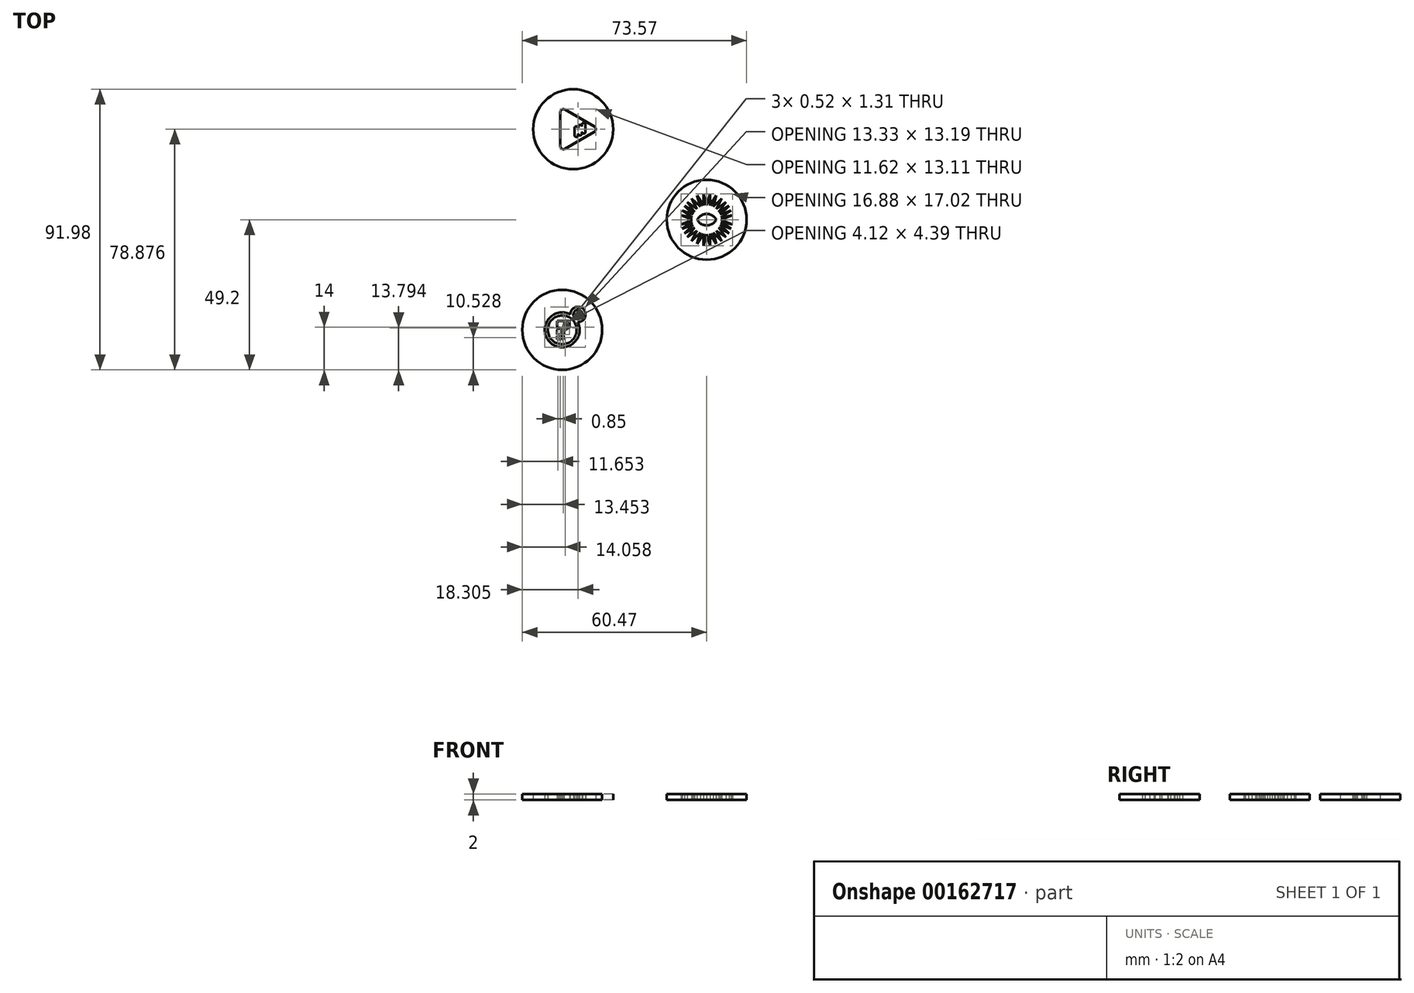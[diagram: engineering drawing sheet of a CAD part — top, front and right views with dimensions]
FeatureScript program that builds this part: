
annotation { "Feature Type Name" : "Feature", "Feature Type Description" : "" }
export const myFeature = defineFeature(function(context is Context, id is Id, definition is map)
    precondition{}
    {
        {
            var Q0;
            Q0=qCreatedBy(makeId("Top.planeOp"),FACE);
            var sketch = newSketch(context, id + "F0", { "sketchPlane" : qUnion([Q0])});
            skCircle(sketch, "E0", {"center": v(0, 0) * mm, "radius": 13.1 * mm});
            skLineSegment(sketch, "E1", {"start": v(0, 4.73) * mm, "end": v(1.07, 8.5) * mm});
            skLineSegment(sketch, "E2", {"start": v(1.07, 8.5) * mm, "end": v(1.07, 4.6) * mm});
            skLineSegment(sketch, "E3", {"start": v(1.07, 4.6) * mm, "end": v(3.18, 7.97) * mm});
            skLineSegment(sketch, "E4", {"start": v(3.18, 7.97) * mm, "end": v(2.11, 4.23) * mm});
            skLineSegment(sketch, "E5", {"start": v(2.11, 4.23) * mm, "end": v(4.97, 7) * mm});
            skLineSegment(sketch, "E6", {"start": v(4.97, 7) * mm, "end": v(3.14, 3.54) * mm});
            skLineSegment(sketch, "E7", {"start": v(3.14, 3.54) * mm, "end": v(6.35, 5.77) * mm});
            skLineSegment(sketch, "E8", {"start": v(6.35, 5.77) * mm, "end": v(3.97, 2.57) * mm});
            skLineSegment(sketch, "E9", {"start": v(3.97, 2.57) * mm, "end": v(7.3, 4.5) * mm});
            skLineSegment(sketch, "E10", {"start": v(7.3, 4.5) * mm, "end": v(4.4, 1.73) * mm});
            skLineSegment(sketch, "E11", {"start": v(4.4, 1.73) * mm, "end": v(8.03, 3) * mm});
            skLineSegment(sketch, "E12", {"start": v(8.03, 3) * mm, "end": v(4.66, 0.79) * mm});
            skLineSegment(sketch, "E13", {"start": v(4.66, 0.79) * mm, "end": v(8.44, 1.53) * mm});
            skLineSegment(sketch, "E14", {"start": v(8.44, 1.53) * mm, "end": v(4.73, 0) * mm});
            skLineSegment(sketch, "E15", {"start": v(4.73, 0) * mm, "end": v(8.58, 0) * mm});
            skLineSegment(sketch, "E16.MirrorCS", {"start": v(-4.73, 0) * mm, "end": v(-8.58, 0) * mm});
            skLineSegment(sketch, "E17.MirrorCS", {"start": v(-8.44, 1.53) * mm, "end": v(-4.73, 0) * mm});
            skLineSegment(sketch, "E18.MirrorCS", {"start": v(-4.66, 0.79) * mm, "end": v(-8.44, 1.53) * mm});
            skLineSegment(sketch, "E19.MirrorCS", {"start": v(-8.03, 3) * mm, "end": v(-4.66, 0.79) * mm});
            skLineSegment(sketch, "E20.MirrorCS", {"start": v(-4.4, 1.73) * mm, "end": v(-8.03, 3) * mm});
            skLineSegment(sketch, "E21.MirrorCS", {"start": v(-7.3, 4.5) * mm, "end": v(-4.4, 1.73) * mm});
            skLineSegment(sketch, "E22.MirrorCS", {"start": v(-3.97, 2.57) * mm, "end": v(-7.3, 4.5) * mm});
            skLineSegment(sketch, "E23.MirrorCS", {"start": v(-6.35, 5.77) * mm, "end": v(-3.97, 2.57) * mm});
            skLineSegment(sketch, "E24.MirrorCS", {"start": v(-3.14, 3.54) * mm, "end": v(-6.35, 5.77) * mm});
            skLineSegment(sketch, "E25.MirrorCS", {"start": v(-4.97, 7) * mm, "end": v(-3.14, 3.54) * mm});
            skLineSegment(sketch, "E26.MirrorCS", {"start": v(-2.11, 4.23) * mm, "end": v(-4.97, 7) * mm});
            skLineSegment(sketch, "E27.MirrorCS", {"start": v(-3.18, 7.97) * mm, "end": v(-2.11, 4.23) * mm});
            skLineSegment(sketch, "E28.MirrorCS", {"start": v(-1.07, 4.6) * mm, "end": v(-3.18, 7.97) * mm});
            skLineSegment(sketch, "E29.MirrorCS", {"start": v(0, 4.73) * mm, "end": v(-1.07, 8.5) * mm});
            skLineSegment(sketch, "E30.MirrorCS", {"start": v(-1.07, 8.5) * mm, "end": v(-1.07, 4.6) * mm});
            skLineSegment(sketch, "E31.MirrorCS", {"start": v(8.44, -1.53) * mm, "end": v(4.73, 0) * mm});
            skLineSegment(sketch, "E32.MirrorCS", {"start": v(4.66, -0.79) * mm, "end": v(8.44, -1.53) * mm});
            skLineSegment(sketch, "E33.MirrorCS", {"start": v(8.03, -3) * mm, "end": v(4.66, -0.79) * mm});
            skLineSegment(sketch, "E34.MirrorCS", {"start": v(4.4, -1.73) * mm, "end": v(8.03, -3) * mm});
            skLineSegment(sketch, "E35.MirrorCS", {"start": v(7.3, -4.5) * mm, "end": v(4.4, -1.73) * mm});
            skLineSegment(sketch, "E36.MirrorCS", {"start": v(3.97, -2.57) * mm, "end": v(7.3, -4.5) * mm});
            skLineSegment(sketch, "E37.MirrorCS", {"start": v(6.35, -5.77) * mm, "end": v(3.97, -2.57) * mm});
            skLineSegment(sketch, "E38.MirrorCS", {"start": v(3.14, -3.54) * mm, "end": v(6.35, -5.77) * mm});
            skLineSegment(sketch, "E39.MirrorCS", {"start": v(4.97, -7) * mm, "end": v(3.14, -3.54) * mm});
            skLineSegment(sketch, "E40.MirrorCS", {"start": v(2.11, -4.23) * mm, "end": v(4.97, -7) * mm});
            skLineSegment(sketch, "E41.MirrorCS", {"start": v(3.18, -7.97) * mm, "end": v(2.11, -4.23) * mm});
            skLineSegment(sketch, "E42.MirrorCS", {"start": v(1.07, -4.6) * mm, "end": v(3.18, -7.97) * mm});
            skLineSegment(sketch, "E43.MirrorCS", {"start": v(1.07, -8.5) * mm, "end": v(1.07, -4.6) * mm});
            skLineSegment(sketch, "E44.MirrorCS", {"start": v(0, -4.73) * mm, "end": v(1.07, -8.5) * mm});
            skLineSegment(sketch, "E45.MirrorCS", {"start": v(0, -4.73) * mm, "end": v(-1.07, -8.5) * mm});
            skLineSegment(sketch, "E46.MirrorCS", {"start": v(-1.07, -8.5) * mm, "end": v(-1.07, -4.6) * mm});
            skLineSegment(sketch, "E47.MirrorCS", {"start": v(-1.07, -4.6) * mm, "end": v(-3.18, -7.97) * mm});
            skLineSegment(sketch, "E48.MirrorCS", {"start": v(-3.18, -7.97) * mm, "end": v(-2.11, -4.23) * mm});
            skLineSegment(sketch, "E49.MirrorCS", {"start": v(-2.11, -4.23) * mm, "end": v(-4.97, -7) * mm});
            skLineSegment(sketch, "E50.MirrorCS", {"start": v(-4.97, -7) * mm, "end": v(-3.14, -3.54) * mm});
            skLineSegment(sketch, "E51.MirrorCS", {"start": v(-3.14, -3.54) * mm, "end": v(-6.35, -5.77) * mm});
            skLineSegment(sketch, "E52.MirrorCS", {"start": v(-6.35, -5.77) * mm, "end": v(-3.97, -2.57) * mm});
            skLineSegment(sketch, "E53.MirrorCS", {"start": v(-3.97, -2.57) * mm, "end": v(-7.3, -4.5) * mm});
            skLineSegment(sketch, "E54.MirrorCS", {"start": v(-7.3, -4.5) * mm, "end": v(-4.4, -1.73) * mm});
            skLineSegment(sketch, "E55.MirrorCS", {"start": v(-4.4, -1.73) * mm, "end": v(-8.03, -3) * mm});
            skLineSegment(sketch, "E56.MirrorCS", {"start": v(-8.03, -3) * mm, "end": v(-4.66, -0.79) * mm});
            skLineSegment(sketch, "E57.MirrorCS", {"start": v(-4.66, -0.79) * mm, "end": v(-8.44, -1.53) * mm});
            skLineSegment(sketch, "E58.MirrorCS", {"start": v(-8.44, -1.53) * mm, "end": v(-4.73, 0) * mm});
            skSolve(sketch);
        }
        {
            var Q0;
            Q0=makeQuery(id+"F0.imprint","IMPRINT",FACE,{"disambiguationData":[TD([[makeQuery(id+"F0.imprint","IMPRINT",EDGE,{"derivedFrom":sQuery(id+"F0.wireOp",EDGE,"E0")}),1.0]])]});
            extrude(context, id + "F1", {"entities" : qUnion([Q0]), "depth" : 2 * mm});
        }
        {
            var Q0;
            Q0=qCreatedBy(makeId("Top.planeOp"),FACE);
            var sketch = newSketch(context, id + "F2", { "sketchPlane" : qUnion([Q0])});
            skCircle(sketch, "E59", {"center": v(-43.77, 29.68) * mm, "radius": 13.1 * mm});
            skCircle(sketch, "E60.cCircle", {"center": v(-43.77, 29.68) * mm, "radius": 8.41 * mm, "construction": true});
            skLineSegment(sketch, "E60.0", {"start": v(-36.85, 28.81) * mm, "end": v(-46.48, 23.25) * mm});
            skLineSegment(sketch, "E60.1", {"start": v(-47.98, 24.12) * mm, "end": v(-47.98, 35.23) * mm});
            skLineSegment(sketch, "E60.2", {"start": v(-46.48, 36.1) * mm, "end": v(-36.85, 30.54) * mm});
            skPoint(sketch, "E61.visualSharp", {"position": v(-47.98, 36.96) * mm});
            skArc(sketch, "E61.filletArc", {"start": v(-46.48, 36.1) * mm, "mid": v(-47.48, 36.1) * mm, "end": v(-47.98, 35.23) * mm});
            skPoint(sketch, "E62.visualSharp", {"position": v(-47.98, 22.39) * mm});
            skArc(sketch, "E62.filletArc", {"start": v(-47.98, 24.12) * mm, "mid": v(-47.48, 23.25) * mm, "end": v(-46.48, 23.25) * mm});
            skPoint(sketch, "E63.visualSharp", {"position": v(-35.35, 29.68) * mm});
            skArc(sketch, "E63.filletArc", {"start": v(-36.85, 28.81) * mm, "mid": v(-36.35, 29.68) * mm, "end": v(-36.85, 30.54) * mm});
            skLineSegment(sketch, "E64.bottom", {"start": v(-40.24, 31.72) * mm, "end": v(-40.37, 31.72) * mm});
            skLineSegment(sketch, "E64.top", {"start": v(-40.24, 28.26) * mm, "end": v(-40.37, 28.26) * mm});
            skLineSegment(sketch, "E64.left", {"start": v(-39.74, 31.22) * mm, "end": v(-39.74, 28.76) * mm});
            skLineSegment(sketch, "E64.right", {"start": v(-40.87, 31.22) * mm, "end": v(-40.87, 30.61) * mm});
            skPoint(sketch, "E65.visualSharp", {"position": v(-40.87, 31.72) * mm});
            skArc(sketch, "E65.filletArc", {"start": v(-40.37, 31.72) * mm, "mid": v(-40.72, 31.57) * mm, "end": v(-40.87, 31.22) * mm});
            skPoint(sketch, "E66.visualSharp", {"position": v(-39.74, 28.26) * mm});
            skArc(sketch, "E66.filletArc", {"start": v(-40.24, 28.26) * mm, "mid": v(-39.88, 28.4) * mm, "end": v(-39.74, 28.76) * mm});
            skPoint(sketch, "E67.visualSharp", {"position": v(-40.87, 28.26) * mm});
            skArc(sketch, "E67.filletArc", {"start": v(-40.87, 28.76) * mm, "mid": v(-40.72, 28.4) * mm, "end": v(-40.37, 28.26) * mm});
            skPoint(sketch, "E68.visualSharp", {"position": v(-39.74, 31.72) * mm});
            skArc(sketch, "E68.filletArc", {"start": v(-39.74, 31.22) * mm, "mid": v(-39.88, 31.57) * mm, "end": v(-40.24, 31.72) * mm});
            skPoint(sketch, "E69", {"position": v(-22.66, 22.26) * mm});
            skLineSegment(sketch, "E70.bottom", {"start": v(-41.45, 31.11) * mm, "end": v(-41.58, 31.11) * mm});
            skLineSegment(sketch, "E70.top", {"start": v(-41.45, 27.66) * mm, "end": v(-41.58, 27.66) * mm});
            skLineSegment(sketch, "E70.left", {"start": v(-40.95, 28.76) * mm, "end": v(-40.95, 28.16) * mm});
            skLineSegment(sketch, "E70.right", {"start": v(-42.08, 30.61) * mm, "end": v(-42.08, 30.12) * mm});
            skPoint(sketch, "E71.visualSharp", {"position": v(-42.08, 31.11) * mm});
            skArc(sketch, "E71.filletArc", {"start": v(-41.58, 31.11) * mm, "mid": v(-41.94, 30.97) * mm, "end": v(-42.08, 30.61) * mm});
            skPoint(sketch, "E72.visualSharp", {"position": v(-40.95, 27.66) * mm});
            skArc(sketch, "E72.filletArc", {"start": v(-41.45, 27.66) * mm, "mid": v(-41.1, 27.8) * mm, "end": v(-40.95, 28.16) * mm});
            skPoint(sketch, "E73.visualSharp", {"position": v(-42.08, 27.66) * mm});
            skArc(sketch, "E73.filletArc", {"start": v(-42.08, 28.16) * mm, "mid": v(-41.94, 27.8) * mm, "end": v(-41.58, 27.66) * mm});
            skPoint(sketch, "E74.visualSharp", {"position": v(-40.95, 31.11) * mm});
            skArc(sketch, "E74.filletArc", {"start": v(-40.95, 30.61) * mm, "mid": v(-41.1, 30.97) * mm, "end": v(-41.45, 31.11) * mm});
            skLineSegment(sketch, "E75.bottom", {"start": v(-42.68, 30.62) * mm, "end": v(-42.81, 30.62) * mm});
            skLineSegment(sketch, "E75.top", {"start": v(-42.68, 27.16) * mm, "end": v(-42.81, 27.16) * mm});
            skLineSegment(sketch, "E75.left", {"start": v(-42.18, 28.16) * mm, "end": v(-42.18, 27.66) * mm});
            skLineSegment(sketch, "E75.right", {"start": v(-43.31, 30.12) * mm, "end": v(-43.31, 27.66) * mm});
            skPoint(sketch, "E76.visualSharp", {"position": v(-43.31, 30.62) * mm});
            skArc(sketch, "E76.filletArc", {"start": v(-42.81, 30.62) * mm, "mid": v(-43.16, 30.47) * mm, "end": v(-43.31, 30.12) * mm});
            skPoint(sketch, "E77.visualSharp", {"position": v(-42.18, 27.16) * mm});
            skArc(sketch, "E77.filletArc", {"start": v(-42.68, 27.16) * mm, "mid": v(-42.33, 27.3) * mm, "end": v(-42.18, 27.66) * mm});
            skPoint(sketch, "E78.visualSharp", {"position": v(-43.31, 27.16) * mm});
            skArc(sketch, "E78.filletArc", {"start": v(-43.31, 27.66) * mm, "mid": v(-43.16, 27.3) * mm, "end": v(-42.81, 27.16) * mm});
            skPoint(sketch, "E79.visualSharp", {"position": v(-42.18, 30.62) * mm});
            skArc(sketch, "E79.filletArc", {"start": v(-42.18, 30.12) * mm, "mid": v(-42.33, 30.47) * mm, "end": v(-42.68, 30.62) * mm});
            skLineSegment(sketch, "E80", {"start": v(-42.08, 28.16) * mm, "end": v(-42.18, 28.16) * mm});
            skLineSegment(sketch, "E81", {"start": v(-42.08, 30.12) * mm, "end": v(-42.18, 30.12) * mm});
            skLineSegment(sketch, "E82", {"start": v(-40.95, 30.61) * mm, "end": v(-40.87, 30.61) * mm});
            skLineSegment(sketch, "E83", {"start": v(-40.95, 28.76) * mm, "end": v(-40.87, 28.76) * mm});
            skSolve(sketch);
        }
        {
            var Q0;
            Q0=makeQuery(id+"F2.imprint","IMPRINT",FACE,{"disambiguationData":[TD([[makeQuery(id+"F2.imprint","IMPRINT",EDGE,{"derivedFrom":sQuery(id+"F2.wireOp",EDGE,"E64.bottom")}),1.0]])]});
            var Q1;
            Q1=makeQuery(id+"F2.imprint","IMPRINT",FACE,{"disambiguationData":[TD([[makeQuery(id+"F2.imprint","IMPRINT",EDGE,{"derivedFrom":sQuery(id+"F2.wireOp",EDGE,"E59")}),1.0]])]});
            extrude(context, id + "F3", {"entities" : qUnion([Q0, Q1]), "depth" : 2 * mm});
        }
        {
            var Q0;
            Q0=qCreatedBy(makeId("Top.planeOp"),FACE);
            var sketch = newSketch(context, id + "F4", { "sketchPlane" : qUnion([Q0])});
            skCircle(sketch, "E84", {"center": v(-47.37, -36.1) * mm, "radius": 13.1 * mm});
            skCircle(sketch, "E85", {"center": v(-42.2, -31.05) * mm, "radius": 1.5 * mm});
            skArc(sketch, "E86", {"start": v(-42.25, -33.55) * mm, "mid": v(-40.42, -29.3) * mm, "end": v(-44.7, -31.04) * mm});
            skCircle(sketch, "E87", {"center": v(-47.37, -36.1) * mm, "radius": 4.72 * mm});
            skArc(sketch, "E88", {"start": v(-44.7, -31.04) * mm, "mid": v(-51.46, -40.1) * mm, "end": v(-42.25, -33.55) * mm});
            skLineSegment(sketch, "E89.bottom", {"start": v(-44.95, -33.21) * mm, "end": v(-49.08, -33.21) * mm});
            skLineSegment(sketch, "E89.top", {"start": v(-44.95, -35.44) * mm, "end": v(-45.79, -35.44) * mm});
            skLineSegment(sketch, "E89.left", {"start": v(-44.95, -33.21) * mm, "end": v(-44.95, -35.44) * mm});
            skLineSegment(sketch, "E89.right", {"start": v(-49.08, -33.21) * mm, "end": v(-49.08, -35.44) * mm});
            skLineSegment(sketch, "E90.bottom", {"start": v(-49.08, -33.21) * mm, "end": v(-46.79, -33.21) * mm});
            skLineSegment(sketch, "E90.top", {"start": v(-49.08, -37.6) * mm, "end": v(-46.79, -37.6) * mm});
            skLineSegment(sketch, "E90.right", {"start": v(-46.79, -36.44) * mm, "end": v(-46.79, -37.6) * mm});
            skLineSegment(sketch, "E91", {"start": v(-49.08, -35.44) * mm, "end": v(-48.1, -35.44) * mm});
            skLineSegment(sketch, "E92", {"start": v(-48.1, -35.44) * mm, "end": v(-49.08, -36.1) * mm});
            skPoint(sketch, "E92.endSnap0", {"position": v(-49.08, -34.33) * mm});
            skLineSegment(sketch, "E93.trimOffspring", {"start": v(-49.08, -36.1) * mm, "end": v(-49.08, -37.6) * mm});
            skLineSegment(sketch, "E94.bottom", {"start": v(-49.08, -38.02) * mm, "end": v(-48.56, -38.02) * mm});
            skLineSegment(sketch, "E94.top", {"start": v(-49.08, -39.33) * mm, "end": v(-48.56, -39.33) * mm});
            skLineSegment(sketch, "E94.left", {"start": v(-49.08, -38.02) * mm, "end": v(-49.08, -39.33) * mm});
            skLineSegment(sketch, "E94.right", {"start": v(-48.56, -38.02) * mm, "end": v(-48.56, -39.33) * mm});
            skLineSegment(sketch, "E95.bottom", {"start": v(-48.23, -38) * mm, "end": v(-47.7, -38) * mm});
            skLineSegment(sketch, "E95.top", {"start": v(-48.23, -39.32) * mm, "end": v(-47.7, -39.32) * mm});
            skLineSegment(sketch, "E95.left", {"start": v(-48.23, -38) * mm, "end": v(-48.23, -39.32) * mm});
            skLineSegment(sketch, "E95.right", {"start": v(-47.7, -38) * mm, "end": v(-47.7, -39.32) * mm});
            skLineSegment(sketch, "E96.bottom", {"start": v(-47.37, -37.98) * mm, "end": v(-46.85, -37.98) * mm});
            skLineSegment(sketch, "E96.top", {"start": v(-47.37, -39.3) * mm, "end": v(-46.85, -39.3) * mm});
            skLineSegment(sketch, "E96.left", {"start": v(-47.37, -37.98) * mm, "end": v(-47.37, -39.3) * mm});
            skLineSegment(sketch, "E96.right", {"start": v(-46.85, -37.98) * mm, "end": v(-46.85, -39.3) * mm});
            skPoint(sketch, "E97.visualSharp", {"position": v(-46.79, -35.44) * mm});
            skArc(sketch, "E97.filletArc", {"start": v(-45.79, -35.44) * mm, "mid": v(-46.5, -35.73) * mm, "end": v(-46.79, -36.44) * mm});
            skSolve(sketch);
        }
        {
            var Q0;
            Q0=makeQuery(id+"F4.imprint","IMPRINT",FACE,{"disambiguationData":[TD([[makeQuery(id+"F4.imprint","IMPRINT",EDGE,{"derivedFrom":sQuery(id+"F4.wireOp",EDGE,"E84")}),1.0]])]});
            var Q1;
            Q1=makeQuery(id+"F4.imprint","IMPRINT",FACE,{"disambiguationData":[TD([[makeQuery(id+"F4.imprint","IMPRINT",EDGE,{"derivedFrom":sQuery(id+"F4.wireOp",EDGE,"E85")}),1.0]])]});
            var Q2;
            Q2=makeQuery(id+"F4.imprint","IMPRINT",FACE,{"disambiguationData":[TD([[makeQuery(id+"F4.imprint","IMPRINT",EDGE,{"derivedFrom":sQuery(id+"F4.wireOp",EDGE,"E87")}),1.0]])]});
            extrude(context, id + "F5", {"entities" : qUnion([Q0, Q1, Q2]), "depth" : 2 * mm});
        }
        {
            var Q0;
            Q0=makeQuery(id+"F1.opExtrude","CAP_FACE",FACE,{"disambiguationData":[OSD([sQuery(id+"F0.wireOp",EDGE,"E0"),sQuery(id+"F0.wireOp",EDGE,"E1"),sQuery(id+"F0.wireOp",EDGE,"E2"),sQuery(id+"F0.wireOp",EDGE,"E3"),sQuery(id+"F0.wireOp",EDGE,"E4"),sQuery(id+"F0.wireOp",EDGE,"E5"),sQuery(id+"F0.wireOp",EDGE,"E6"),sQuery(id+"F0.wireOp",EDGE,"E7"),sQuery(id+"F0.wireOp",EDGE,"E8"),sQuery(id+"F0.wireOp",EDGE,"E9"),sQuery(id+"F0.wireOp",EDGE,"E10"),sQuery(id+"F0.wireOp",EDGE,"E11"),sQuery(id+"F0.wireOp",EDGE,"E12"),sQuery(id+"F0.wireOp",EDGE,"E13"),sQuery(id+"F0.wireOp",EDGE,"E14"),sQuery(id+"F0.wireOp",EDGE,"E19.MirrorCS"),sQuery(id+"F0.wireOp",EDGE,"E20.MirrorCS"),sQuery(id+"F0.wireOp",EDGE,"E21.MirrorCS"),sQuery(id+"F0.wireOp",EDGE,"E22.MirrorCS"),sQuery(id+"F0.wireOp",EDGE,"E23.MirrorCS"),sQuery(id+"F0.wireOp",EDGE,"E24.MirrorCS"),sQuery(id+"F0.wireOp",EDGE,"E25.MirrorCS"),sQuery(id+"F0.wireOp",EDGE,"E26.MirrorCS"),sQuery(id+"F0.wireOp",EDGE,"E27.MirrorCS"),sQuery(id+"F0.wireOp",EDGE,"E28.MirrorCS"),sQuery(id+"F0.wireOp",EDGE,"E29.MirrorCS"),sQuery(id+"F0.wireOp",EDGE,"E30.MirrorCS"),sQuery(id+"F0.wireOp",EDGE,"E18.MirrorCS"),sQuery(id+"F0.wireOp",EDGE,"E17.MirrorCS"),sQuery(id+"F0.wireOp",EDGE,"E31.MirrorCS"),sQuery(id+"F0.wireOp",EDGE,"E32.MirrorCS"),sQuery(id+"F0.wireOp",EDGE,"E33.MirrorCS"),sQuery(id+"F0.wireOp",EDGE,"E34.MirrorCS"),sQuery(id+"F0.wireOp",EDGE,"E35.MirrorCS"),sQuery(id+"F0.wireOp",EDGE,"E36.MirrorCS"),sQuery(id+"F0.wireOp",EDGE,"E37.MirrorCS"),sQuery(id+"F0.wireOp",EDGE,"E38.MirrorCS"),sQuery(id+"F0.wireOp",EDGE,"E39.MirrorCS"),sQuery(id+"F0.wireOp",EDGE,"E40.MirrorCS"),sQuery(id+"F0.wireOp",EDGE,"E41.MirrorCS"),sQuery(id+"F0.wireOp",EDGE,"E42.MirrorCS"),sQuery(id+"F0.wireOp",EDGE,"E43.MirrorCS"),sQuery(id+"F0.wireOp",EDGE,"E44.MirrorCS"),sQuery(id+"F0.wireOp",EDGE,"E45.MirrorCS"),sQuery(id+"F0.wireOp",EDGE,"E46.MirrorCS"),sQuery(id+"F0.wireOp",EDGE,"E47.MirrorCS"),sQuery(id+"F0.wireOp",EDGE,"E48.MirrorCS"),sQuery(id+"F0.wireOp",EDGE,"E49.MirrorCS"),sQuery(id+"F0.wireOp",EDGE,"E50.MirrorCS"),sQuery(id+"F0.wireOp",EDGE,"E51.MirrorCS"),sQuery(id+"F0.wireOp",EDGE,"E52.MirrorCS"),sQuery(id+"F0.wireOp",EDGE,"E53.MirrorCS"),sQuery(id+"F0.wireOp",EDGE,"E54.MirrorCS"),sQuery(id+"F0.wireOp",EDGE,"E55.MirrorCS"),sQuery(id+"F0.wireOp",EDGE,"E56.MirrorCS"),sQuery(id+"F0.wireOp",EDGE,"E57.MirrorCS"),sQuery(id+"F0.wireOp",EDGE,"E58.MirrorCS")])],"isStart":false});
            var sketch = newSketch(context, id + "F6", { "sketchPlane" : qUnion([Q0])});
            skArc(sketch, "E98", {"start": v(-3.11, 0) * mm, "mid": v(0.02, -1.88) * mm, "end": v(3.15, 0) * mm});
            skArc(sketch, "E99.MirrorCS", {"start": v(-3.11, 0) * mm, "mid": v(0.02, 1.88) * mm, "end": v(3.15, 0) * mm});
            skSolve(sketch);
        }
        {
            var Q0;
            Q0=makeQuery(id+"F6.imprint","IMPRINT",FACE,{"disambiguationData":[TD([[makeQuery(id+"F6.imprint","IMPRINT",EDGE,{"derivedFrom":sQuery(id+"F6.wireOp",EDGE,"E98")}),1.0]])]});
            extrude(context, id + "F7", {"entities" : qUnion([Q0]), "oppositeDirection" : true, "depth" : 2 * mm});
        }
    });
